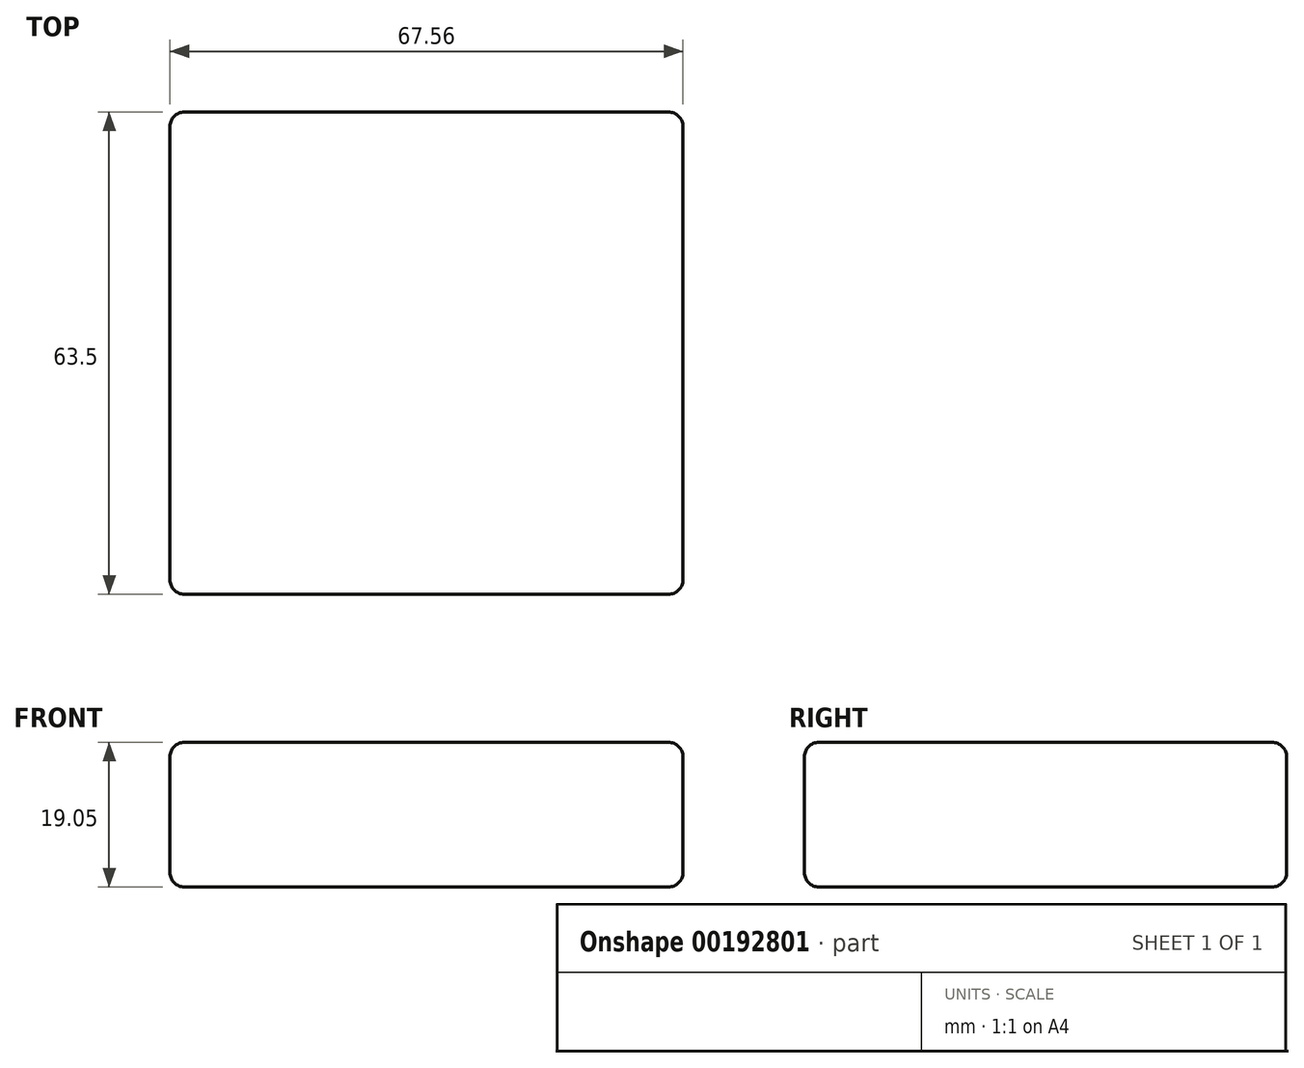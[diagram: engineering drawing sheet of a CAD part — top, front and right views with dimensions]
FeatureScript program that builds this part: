
annotation { "Feature Type Name" : "Feature", "Feature Type Description" : "" }
export const myFeature = defineFeature(function(context is Context, id is Id, definition is map)
    precondition{}
    {
        {
            var Q0;
            Q0=qCreatedBy(makeId("Top.planeOp"),FACE);
            var sketch = newSketch(context, id + "F0", { "sketchPlane" : qUnion([Q0])});
            skLineSegment(sketch, "E0.bottom", {"start": v(-33.78, 31.75) * mm, "end": v(33.78, 31.75) * mm});
            skLineSegment(sketch, "E0.top", {"start": v(-33.78, -31.75) * mm, "end": v(33.78, -31.75) * mm});
            skLineSegment(sketch, "E0.left", {"start": v(-33.78, 31.75) * mm, "end": v(-33.78, -31.75) * mm});
            skLineSegment(sketch, "E0.right", {"start": v(33.78, 31.75) * mm, "end": v(33.78, -31.75) * mm});
            skLineSegment(sketch, "E1", {"start": v(-33.78, 31.75) * mm, "end": v(33.78, -31.75) * mm, "construction": true});
            skSolve(sketch);
        }
        {
            var Q0;
            Q0=qSketchRegion(id+"F0",true);
            extrude(context, id + "F1", {"entities" : qUnion([Q0]), "depth" : 19.05 * mm});
        }
        {
            var Q0;
            Q0=makeQuery(id+"F1.opExtrude","CAP_FACE",FACE,{"disambiguationData":[OSD([sQuery(id+"F0.wireOp",EDGE,"E0.bottom"),sQuery(id+"F0.wireOp",EDGE,"E0.top"),sQuery(id+"F0.wireOp",EDGE,"E0.left"),sQuery(id+"F0.wireOp",EDGE,"E0.right")])],"isStart":false});
            var Q1;
            Q1=makeQuery(id+"F1.opExtrude","CAP_FACE",FACE,{"disambiguationData":[OSD([sQuery(id+"F0.wireOp",EDGE,"E0.bottom"),sQuery(id+"F0.wireOp",EDGE,"E0.top"),sQuery(id+"F0.wireOp",EDGE,"E0.left"),sQuery(id+"F0.wireOp",EDGE,"E0.right")])],"isStart":true});
            var Q2;
            Q2=makeQuery(id+"F1.opExtrude","SWEPT_EDGE",EDGE,{"disambiguationData":[OSD([sQuery(id+"F0.wireOp",EDGE,"E0.bottom"),sQuery(id+"F0.wireOp",EDGE,"E0.right")])]});
            var Q3;
            Q3=makeQuery(id+"F1.opExtrude","SWEPT_EDGE",EDGE,{"disambiguationData":[OSD([sQuery(id+"F0.wireOp",EDGE,"E0.top"),sQuery(id+"F0.wireOp",EDGE,"E0.right")])]});
            var Q4;
            Q4=makeQuery(id+"F1.opExtrude","SWEPT_EDGE",EDGE,{"disambiguationData":[OSD([sQuery(id+"F0.wireOp",EDGE,"E0.top"),sQuery(id+"F0.wireOp",EDGE,"E0.left")])]});
            var Q5;
            Q5=makeQuery(id+"F1.opExtrude","SWEPT_EDGE",EDGE,{"disambiguationData":[OSD([sQuery(id+"F0.wireOp",EDGE,"E0.bottom"),sQuery(id+"F0.wireOp",EDGE,"E0.left")])]});
            fillet(context, id + "F2", {"entities" : qUnion([Q0, Q1, Q2, Q3, Q4, Q5]), "radius" : 1.9 * mm, "tangentPropagation" : true, "allowEdgeOverflow" : false});
        }
    });
